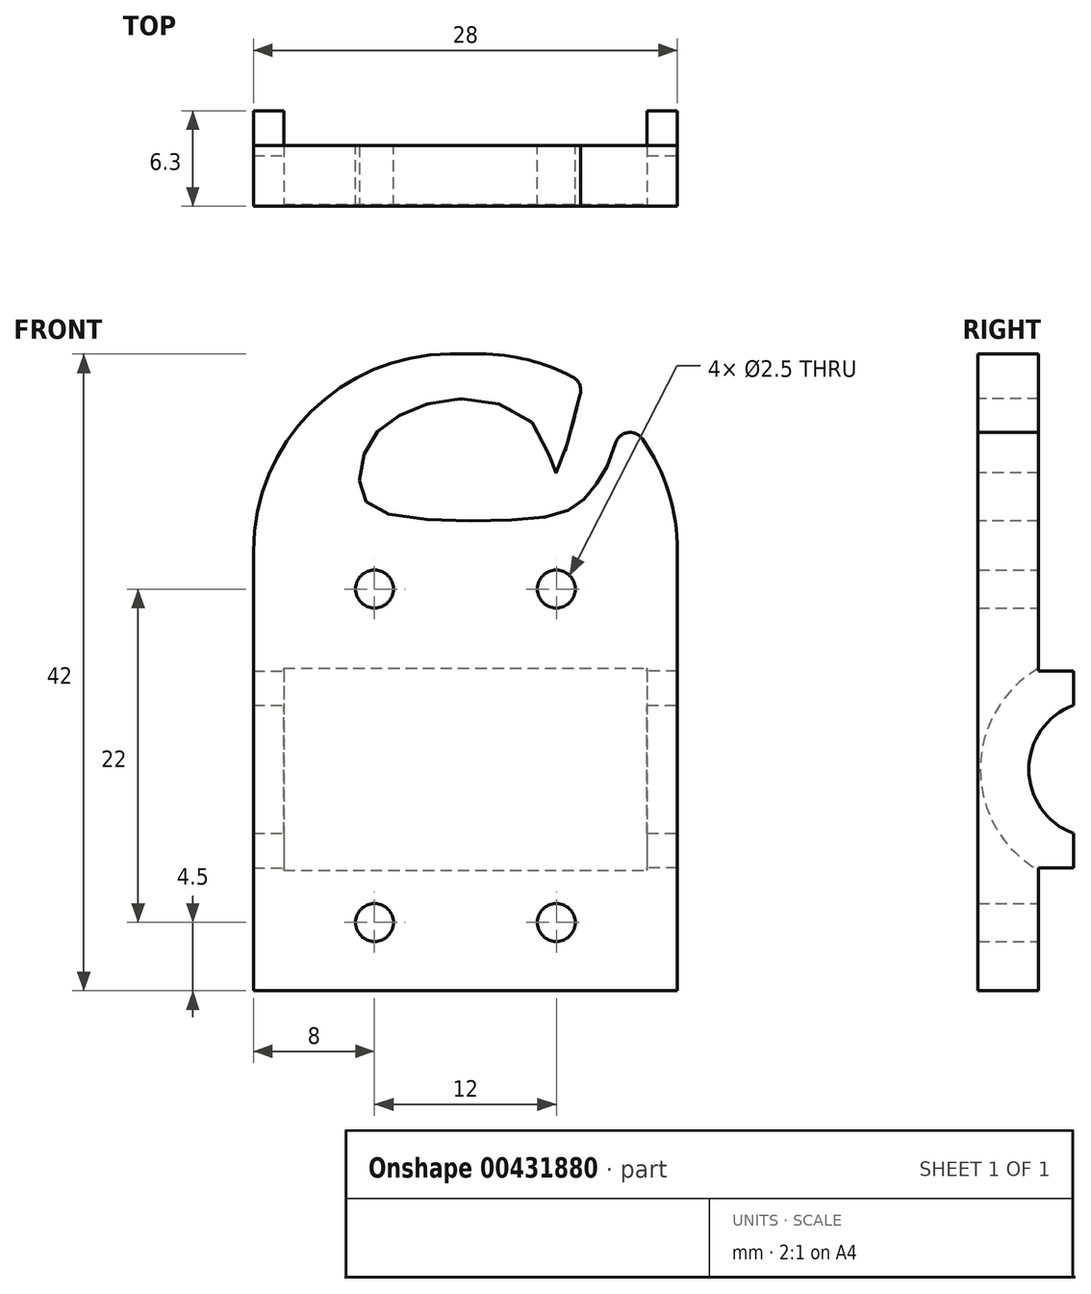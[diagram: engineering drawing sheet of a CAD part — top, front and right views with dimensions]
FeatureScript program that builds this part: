
annotation { "Feature Type Name" : "Feature", "Feature Type Description" : "" }
export const myFeature = defineFeature(function(context is Context, id is Id, definition is map)
    precondition{}
    {
        {
            var Q0;
            Q0=qCreatedBy(makeId("Front.planeOp"),FACE);
            var sketch = newSketch(context, id + "F0", { "sketchPlane" : qUnion([Q0])});
            skLineSegment(sketch, "E0.bottom", {"start": v(28, 42) * mm, "end": v(0, 42) * mm});
            skLineSegment(sketch, "E0.top", {"start": v(28, 0) * mm, "end": v(0, 0) * mm});
            skLineSegment(sketch, "E0.left", {"start": v(28, 42) * mm, "end": v(28, 0) * mm});
            skLineSegment(sketch, "E0.right", {"start": v(0, 42) * mm, "end": v(0, 0) * mm});
            skSolve(sketch);
        }
        {
            var Q0;
            Q0=makeQuery(id+"F0.imprint","IMPRINT",FACE,{"disambiguationData":[TD([[makeQuery(id+"F0.imprint","IMPRINT",EDGE,{"derivedFrom":sQuery(id+"F0.wireOp",EDGE,"E0.bottom")}),1.0]])]});
            extrude(context, id + "F1", {"entities" : qUnion([Q0]), "depth" : 4 * mm});
        }
        {
            var Q0;
            Q0=makeQuery(id+"F1.opExtrude","CAP_FACE",FACE,{"disambiguationData":[OSD([sQuery(id+"F0.wireOp",EDGE,"E0.bottom"),sQuery(id+"F0.wireOp",EDGE,"E0.top"),sQuery(id+"F0.wireOp",EDGE,"E0.left"),sQuery(id+"F0.wireOp",EDGE,"E0.right")])],"isStart":true});
            var sketch = newSketch(context, id + "F2", { "sketchPlane" : qUnion([Q0])});
            skLineSegment(sketch, "E1.bottom", {"start": v(-28, 21.1) * mm, "end": v(-26, 21.1) * mm});
            skLineSegment(sketch, "E1.top", {"start": v(-28, 8.1) * mm, "end": v(-26, 8.1) * mm});
            skLineSegment(sketch, "E1.left", {"start": v(-28, 21.1) * mm, "end": v(-28, 8.1) * mm});
            skLineSegment(sketch, "E1.right", {"start": v(-26, 21.1) * mm, "end": v(-26, 8.1) * mm});
            skLineSegment(sketch, "E2.bottom", {"start": v(0, 21.1) * mm, "end": v(-2, 21.1) * mm});
            skLineSegment(sketch, "E2.top", {"start": v(0, 8.1) * mm, "end": v(-2, 8.1) * mm});
            skLineSegment(sketch, "E2.left", {"start": v(0, 21.1) * mm, "end": v(0, 8.1) * mm});
            skLineSegment(sketch, "E2.right", {"start": v(-2, 21.1) * mm, "end": v(-2, 8.1) * mm});
            skLineSegment(sketch, "E3", {"start": v(-28, 8.1) * mm, "end": v(0, 8.1) * mm, "construction": true});
            skSolve(sketch);
        }
        {
            var Q0;
            Q0=makeQuery(id+"F2.imprint","IMPRINT",FACE,{"disambiguationData":[TD([[makeQuery(id+"F2.imprint","IMPRINT",EDGE,{"derivedFrom":sQuery(id+"F2.wireOp",EDGE,"E1.bottom")}),-1.0]])]});
            var Q1;
            Q1=makeQuery(id+"F2.imprint","IMPRINT",FACE,{"disambiguationData":[TD([[makeQuery(id+"F2.imprint","IMPRINT",EDGE,{"derivedFrom":sQuery(id+"F2.wireOp",EDGE,"E2.bottom")}),1.0]])]});
            extrude(context, id + "F3", {"entities" : qUnion([Q0, Q1]), "operationType" : NewBodyOperationType.ADD, "depth" : 2.3 * mm});
        }
        {
            var Q0;
            Q0=makeQuery(id+"F3.boolean.opBoolean","MERGE",FACE,{"derivedFrom":[makeQuery(id+"F1.opExtrude","SWEPT_FACE",FACE,{"disambiguationData":[OSD([sQuery(id+"F0.wireOp",EDGE,"E0.left")])]}),makeQuery(id+"F3.opExtrude","SWEPT_FACE",FACE,{"disambiguationData":[OSD([sQuery(id+"F2.wireOp",EDGE,"E1.left")])]})]});
            var sketch = newSketch(context, id + "F4", { "sketchPlane" : qUnion([Q0])});
            skCircle(sketch, "E4", {"center": v(3.85, 14.6) * mm, "radius": 7.55 * mm, "construction": true});
            skLineSegment(sketch, "E5", {"start": v(0, 21.1) * mm, "end": v(0, 8.1) * mm, "construction": true});
            skCircle(sketch, "E6", {"center": v(3.85, 14.6) * mm, "radius": 4.5 * mm});
            skLineSegment(sketch, "E7", {"start": v(-3.7, 21.23) * mm, "end": v(-3.7, 12.68) * mm, "construction": true});
            skLineSegment(sketch, "E8", {"start": v(2.3, 14.6) * mm, "end": v(3.85, 14.6) * mm, "construction": true});
            skSolve(sketch);
        }
        {
            var Q0;
            Q0=makeQuery(id+"F4.imprint","IMPRINT",FACE,{"disambiguationData":[TD([[makeQuery(id+"F4.imprint","IMPRINT",EDGE,{"derivedFrom":sQuery(id+"F4.wireOp",EDGE,"E6")}),1.0]])]});
            var Q1;
            Q1=makeQuery(id+"F1.opExtrude","SWEPT_BODY",BODY,{"disambiguationData":[OSD([sQuery(id+"F0.wireOp",EDGE,"E0.bottom"),sQuery(id+"F0.wireOp",EDGE,"E0.top"),sQuery(id+"F0.wireOp",EDGE,"E0.left"),sQuery(id+"F0.wireOp",EDGE,"E0.right")])]});
            extrude(context, id + "F5", {"entities" : qUnion([Q0]), "operationType" : NewBodyOperationType.REMOVE, "endBound" : BoundingType.UP_TO_BODY, "oppositeDirection" : true, "endBoundEntityBody" : qUnion([Q1]), "depth" : 35 * mm});
        }
        {
            var Q0;
            Q0=makeQuery(id+"F4.imprint","IMPRINT",FACE,{"disambiguationData":[TD([[makeQuery(id+"F4.imprint","IMPRINT",EDGE,{"derivedFrom":sQuery(id+"F4.wireOp",EDGE,"E6")}),-1.0]])]});
            cPlane(context, id + "F6", {"entities" : qUnion([Q0]), "cplaneType" : CPlaneType.OFFSET, "offset" : 2 * mm, "oppositeDirection" : true, "width" : 150 * mm, "height" : 150 * mm});
        }
        {
            var Q0;
            Q0=qCreatedBy(id+"F6.planeOp",FACE);
            var sketch = newSketch(context, id + "F7", { "sketchPlane" : qUnion([Q0])});
            skCircle(sketch, "E9", {"center": v(3.85, 14.6) * mm, "radius": 7.7 * mm});
            skSolve(sketch);
        }
        {
            var Q0;
            Q0=makeQuery(id+"F7.imprint","IMPRINT",FACE,{"disambiguationData":[TD([[makeQuery(id+"F7.imprint","IMPRINT",EDGE,{"derivedFrom":sQuery(id+"F7.wireOp",EDGE,"E9")}),1.0]])]});
            extrude(context, id + "F8", {"entities" : qUnion([Q0]), "operationType" : NewBodyOperationType.REMOVE, "oppositeDirection" : true, "depth" : 24 * mm});
        }
        {
            var Q0;
            Q0=makeQuery(id+"F1.opExtrude","CAP_FACE",FACE,{"disambiguationData":[OSD([sQuery(id+"F0.wireOp",EDGE,"E0.bottom"),sQuery(id+"F0.wireOp",EDGE,"E0.top"),sQuery(id+"F0.wireOp",EDGE,"E0.left"),sQuery(id+"F0.wireOp",EDGE,"E0.right")])],"isStart":false});
            var sketch = newSketch(context, id + "F9", { "sketchPlane" : qUnion([Q0])});
            skLineSegment(sketch, "E10", {"start": v(0, 26.5) * mm, "end": v(28, 26.5) * mm, "construction": true});
            skLineSegment(sketch, "E11", {"start": v(20, 0) * mm, "end": v(20, 42) * mm, "construction": true});
            skLineSegment(sketch, "E12", {"start": v(8, 0) * mm, "end": v(8, 42) * mm, "construction": true});
            skLineSegment(sketch, "E13", {"start": v(0, 15.5) * mm, "end": v(28, 15.5) * mm, "construction": true});
            skPoint(sketch, "E14", {"position": v(8, 26.5) * mm});
            skPoint(sketch, "E15", {"position": v(20, 26.5) * mm});
            skPoint(sketch, "E16.MirrorP", {"position": v(8, 4.5) * mm});
            skPoint(sketch, "E17.MirrorP", {"position": v(20, 4.5) * mm});
            skSolve(sketch);
        }
        {
            var Q0;
            Q0=sQuery(id+"F9.wireOp",VERTEX,"E14");
            var Q1;
            Q1=sQuery(id+"F9.wireOp",VERTEX,"E15");
            var Q2;
            Q2=sQuery(id+"F9.wireOp",VERTEX,"E17.MirrorP");
            var Q3;
            Q3=sQuery(id+"F9.wireOp",VERTEX,"E16.MirrorP");
            var Q4;
            Q4=makeQuery(id+"F1.opExtrude","SWEPT_BODY",BODY,{"disambiguationData":[OSD([sQuery(id+"F0.wireOp",EDGE,"E0.bottom"),sQuery(id+"F0.wireOp",EDGE,"E0.top"),sQuery(id+"F0.wireOp",EDGE,"E0.left"),sQuery(id+"F0.wireOp",EDGE,"E0.right")])]});
            hole(context, id + "F10", {"style" : HoleStyle.SIMPLE, "endStyle" : HoleEndStyle.THROUGH, "holeDiameter" : 2.5 * mm, "isTappedThrough" : true, "tappedDepth" : 12 * mm, "tapClearance" : 3, "locations" : qUnion([Q0, Q1, Q2, Q3]), "scope" : qUnion([Q4]), "startStyle" : HoleStartStyle.PART});
        }
        {
            var Q0;
            Q0=makeQuery(id+"F1.opExtrude","SWEPT_EDGE",EDGE,{"disambiguationData":[OSD([sQuery(id+"F0.wireOp",EDGE,"E0.bottom"),sQuery(id+"F0.wireOp",EDGE,"E0.left")])]});
            var Q1;
            Q1=makeQuery(id+"F1.opExtrude","SWEPT_EDGE",EDGE,{"disambiguationData":[OSD([sQuery(id+"F0.wireOp",EDGE,"E0.bottom"),sQuery(id+"F0.wireOp",EDGE,"E0.right")])]});
            fillet(context, id + "F11", {"entities" : qUnion([Q0, Q1]), "radius" : 13 * mm, "tangentPropagation" : true, "allowEdgeOverflow" : false});
        }
        {
            var Q0;
            {var subQ3=sQuery(id+"F2.wireOp",EDGE,"E1.bottom");Q0=makeQuery(id+"F2.imprint","IMPRINT",FACE,{"disambiguationData":[TD([[makeQuery(id+"F2.imprint","IMPRINT",EDGE,{"derivedFrom":subQ3}),1.0]])]});}
            var sketch = newSketch(context, id + "F12", { "sketchPlane" : qUnion([Q0])});
            skLineSegment(sketch, "E18", {"start": v(0, 31) * mm, "end": v(-28, 31) * mm, "construction": true});
            skLineSegment(sketch, "E19", {"start": v(-14, 45.16) * mm, "end": v(-14, 31) * mm, "construction": true});
            skArc(sketch, "E20", {"start": v(-21.85, 40.32) * mm, "mid": v(-23.16, 39.57) * mm, "end": v(-24.37, 38.68) * mm});
            skFitSpline(sketch, "E21", {"points": [v(-24.37, 38.68) * mm, v(-23.34, 34.6) * mm, v(-22.43, 33.14) * mm, v(-21.37, 32.02) * mm, v(-19.55, 31.31) * mm, v(-14, 31) * mm, v(-8.03, 31.78) * mm, v(-7.02, 33.38) * mm, v(-7.67, 36.17) * mm, v(-9.8, 38.03) * mm, v(-14, 39.04) * mm, v(-18.99, 36.74) * mm, v(-19.97, 34.17) * mm, v(-21.4, 38.68) * mm, v(-21.85, 40.32) * mm], "startDerivative": vector(11.4, -85.18) * mm, "endDerivative": vector(-27.02, 94.55) * mm});
            skSolve(sketch);
        }
        {
            var Q0;
            Q0=qSketchRegion(id+"F12",true);
            extrude(context, id + "F13", {"entities" : qUnion([Q0]), "operationType" : NewBodyOperationType.REMOVE, "oppositeDirection" : true, "depth" : 25 * mm});
        }
        {
            var Q0;
            Q0=makeQuery(id+"F13.boolean.opBoolean","INTERSECT",EDGE,{"disambiguationData":[OD(0.0)],"derivedFrom":[makeQuery(id+"F11.opFillet","BLEND_FACE",FACE,{"disambiguationData":[OSD([sQuery(id+"F0.wireOp",EDGE,"E0.bottom"),sQuery(id+"F0.wireOp",EDGE,"E0.left")])]}),makeQuery(id+"F13.opExtrude","SWEPT_FACE",FACE,{"disambiguationData":[OSD([sQuery(id+"F12.wireOp",EDGE,"E21")])]})]});
            var Q1;
            Q1=makeQuery(id+"F13.boolean.opBoolean","INTERSECT",EDGE,{"disambiguationData":[OD(1.0)],"derivedFrom":[makeQuery(id+"F11.opFillet","BLEND_FACE",FACE,{"disambiguationData":[OSD([sQuery(id+"F0.wireOp",EDGE,"E0.bottom"),sQuery(id+"F0.wireOp",EDGE,"E0.left")])]}),makeQuery(id+"F13.opExtrude","SWEPT_FACE",FACE,{"disambiguationData":[OSD([sQuery(id+"F12.wireOp",EDGE,"E21")])]})]});
            fillet(context, id + "F14", {"entities" : qUnion([Q0, Q1]), "radius" : 1 * mm, "tangentPropagation" : true, "allowEdgeOverflow" : false});
        }
    });
